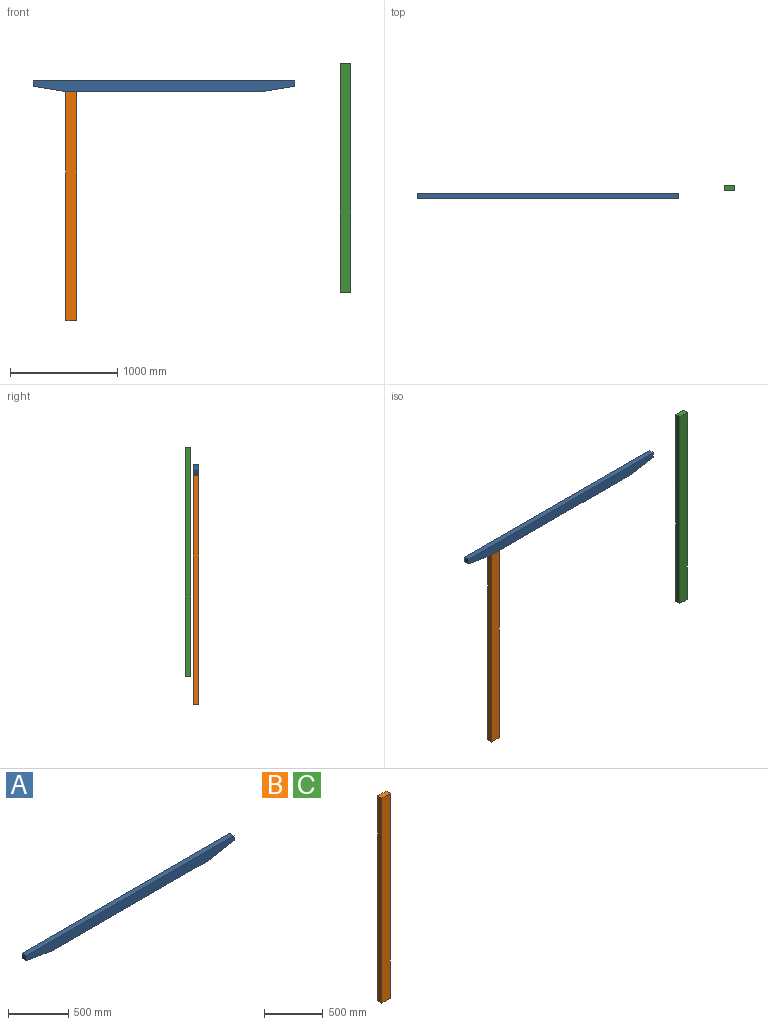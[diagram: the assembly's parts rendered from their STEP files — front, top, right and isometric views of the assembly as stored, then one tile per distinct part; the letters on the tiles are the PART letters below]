
ASSEMBLY  parts=3 mates=1
PART A: 8 faces, bbox 2438.4x50.8x101.6 mm
  f0: plane 2438.4x50.8mm, normal (0,0,1), area 123870.7mm2, adj f1,f5,f6,f7
  f1: plane 50.8x50.8mm, normal (-1,0,0), area 2580.6mm2, adj f0,f2,f6,f7
  f2: plane 304.8x50.8mm, normal (-0.16,0,-0.99), area 15697.4mm2, adj f1,f3,f6,f7
  f3: plane 1828.8x50.8mm, normal (0,0,-1), area 92903mm2, adj f2,f4,f6,f7
  f4: plane 304.8x50.8mm, normal (0.16,0,-0.99), area 15697.4mm2, adj f3,f5,f6,f7
  f5: plane 50.8x50.8mm, normal (1,0,0), area 2580.6mm2, adj f0,f4,f6,f7
  f6: plane 2438.4x101.6mm, normal (0,1,0), area 232257.6mm2, adj f0,f1,f2,f3,f4,f5
  f7: plane 2438.4x101.6mm, normal (0,-1,0), area 232257.6mm2, adj f0,f1,f2,f3,f4,f5
PART B: 6 faces, bbox 101.6x50.8x2133.6 mm
  f0: plane 2133.6x101.6mm, normal (0,1,0), area 216773.8mm2, adj f1,f3,f4,f5
  f1: plane 2133.6x50.8mm, normal (-1,0,0), area 108386.9mm2, adj f0,f2,f4,f5
  f2: plane 2133.6x101.6mm, normal (0,-1,0), area 216773.8mm2, adj f1,f3,f4,f5
  f3: plane 2133.6x50.8mm, normal (1,0,0), area 108386.9mm2, adj f0,f2,f4,f5
  f4: plane 101.6x50.8mm, normal (0,0,1), area 5161.3mm2, adj f0,f1,f2,f3
  f5: plane 101.6x50.8mm, normal (0,0,-1), area 5161.3mm2, adj f0,f1,f2,f3
PART C: same geometry as B
PLACE A t=(-2373.99,465.16,1287.39)mm
PLACE B t=(-2069.19,515.53,-947.81)mm
PLACE C t=(486.99,590.97,-684.19)mm
MATE parallel A.f7 <-> B.f2  axis (0,-1,0) through (-1154.79,465.16,1238.85)mm
